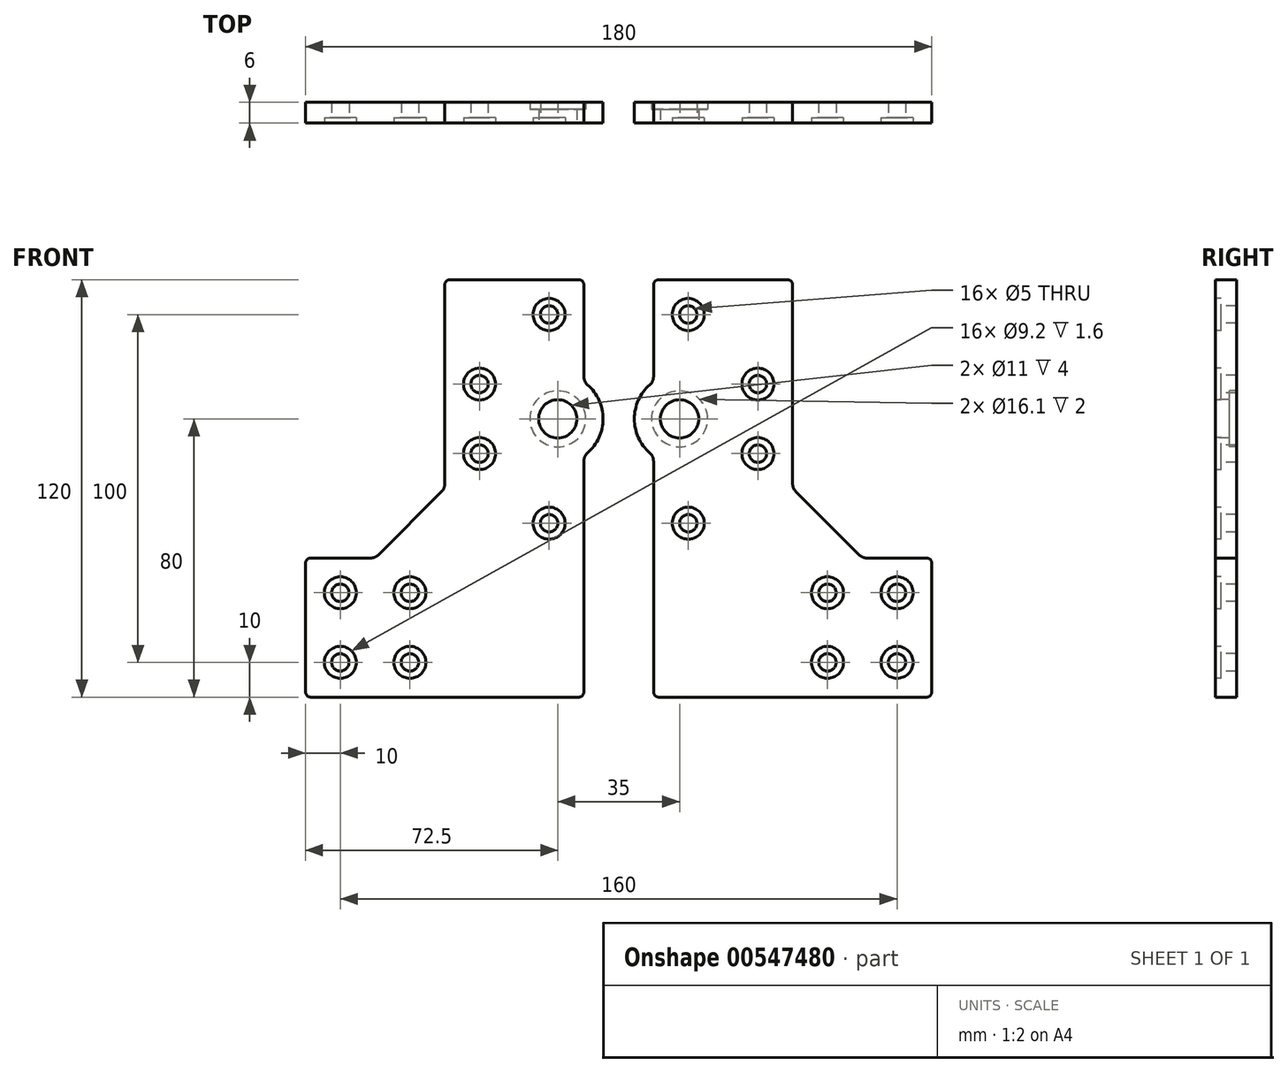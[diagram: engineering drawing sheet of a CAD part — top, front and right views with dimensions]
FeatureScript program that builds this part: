
annotation { "Feature Type Name" : "Feature", "Feature Type Description" : "" }
export const myFeature = defineFeature(function(context is Context, id is Id, definition is map)
    precondition{}
    {
        {
            var Q0;
            Q0=qCreatedBy(makeId("Front.planeOp"),FACE);
            var sketch = newSketch(context, id + "F0", { "sketchPlane" : qUnion([Q0])});
            skCircle(sketch, "E0", {"center": v(-80, -70) * mm, "radius": 2.5 * mm});
            skCircle(sketch, "E1", {"center": v(-80, -70) * mm, "radius": 4.6 * mm});
            skCircle(sketch, "E2.0.1.0", {"center": v(-80, -50) * mm, "radius": 2.5 * mm});
            skCircle(sketch, "E2.0.1.1", {"center": v(-80, -50) * mm, "radius": 4.6 * mm});
            skCircle(sketch, "E2.1.0.0", {"center": v(-60, -70) * mm, "radius": 2.5 * mm});
            skCircle(sketch, "E2.1.0.1", {"center": v(-60, -70) * mm, "radius": 4.6 * mm});
            skCircle(sketch, "E2.1.1.0", {"center": v(-60, -50) * mm, "radius": 2.5 * mm});
            skCircle(sketch, "E2.1.1.1", {"center": v(-60, -50) * mm, "radius": 4.6 * mm});
            skCircle(sketch, "E2.2.3.0", {"center": v(-40, -10) * mm, "radius": 2.5 * mm});
            skCircle(sketch, "E2.2.3.1", {"center": v(-40, -10) * mm, "radius": 4.6 * mm});
            skCircle(sketch, "E2.2.4.0", {"center": v(-40, 10) * mm, "radius": 2.5 * mm});
            skCircle(sketch, "E2.2.4.1", {"center": v(-40, 10) * mm, "radius": 4.6 * mm});
            skCircle(sketch, "E2.3.2.0", {"center": v(-20, -30) * mm, "radius": 2.5 * mm});
            skCircle(sketch, "E2.3.2.1", {"center": v(-20, -30) * mm, "radius": 4.6 * mm});
            skCircle(sketch, "E2.3.5.0", {"center": v(-20, 30) * mm, "radius": 2.5 * mm});
            skCircle(sketch, "E2.3.5.1", {"center": v(-20, 30) * mm, "radius": 4.6 * mm});
            skLineSegment(sketch, "E2.direction1", {"start": v(-80, -70) * mm, "end": v(-60, -70) * mm, "construction": true});
            skLineSegment(sketch, "E2.direction2", {"start": v(-80, -70) * mm, "end": v(-80, -50) * mm, "construction": true});
            skLineSegment(sketch, "E3", {"start": v(-90, -80) * mm, "end": v(-10, -80) * mm});
            skLineSegment(sketch, "E4", {"start": v(-10, -80) * mm, "end": v(-10, -10.62) * mm});
            skLineSegment(sketch, "E5", {"start": v(-10, 40) * mm, "end": v(-50, 40) * mm});
            skLineSegment(sketch, "E6", {"start": v(-50, 40) * mm, "end": v(-50, -20) * mm});
            skLineSegment(sketch, "E7", {"start": v(-70, -40) * mm, "end": v(-90, -40) * mm});
            skLineSegment(sketch, "E8", {"start": v(-90, -40) * mm, "end": v(-90, -80) * mm});
            skCircle(sketch, "E9", {"center": v(-17.5, 0) * mm, "radius": 5.5 * mm});
            skCircle(sketch, "E10", {"center": v(-17.5, 0) * mm, "radius": 8.05 * mm});
            skArc(sketch, "E11", {"start": v(-10, -10.62) * mm, "mid": v(-4.5, 0) * mm, "end": v(-10, 10.62) * mm});
            skLineSegment(sketch, "E12.trimOffspring", {"start": v(-10, 10.62) * mm, "end": v(-10, 40) * mm});
            skLineSegment(sketch, "E13", {"start": v(-70, -40) * mm, "end": v(-50, -20) * mm});
            skSolve(sketch);
        }
        {
            var Q0;
            Q0=makeQuery(id+"F0.imprint","IMPRINT",FACE,{"disambiguationData":[TD([[makeQuery(id+"F0.imprint","IMPRINT",EDGE,{"derivedFrom":sQuery(id+"F0.wireOp",EDGE,"E1")}),-1.0]])]});
            var Q1;
            Q1=makeQuery(id+"F0.imprint","IMPRINT",FACE,{"disambiguationData":[TD([[makeQuery(id+"F0.imprint","IMPRINT",EDGE,{"derivedFrom":sQuery(id+"F0.wireOp",EDGE,"E2.3.5.0")}),-1.0]])]});
            var Q2;
            Q2=makeQuery(id+"F0.imprint","IMPRINT",FACE,{"disambiguationData":[TD([[makeQuery(id+"F0.imprint","IMPRINT",EDGE,{"derivedFrom":sQuery(id+"F0.wireOp",EDGE,"E2.2.4.0")}),-1.0]])]});
            var Q3;
            Q3=makeQuery(id+"F0.imprint","IMPRINT",FACE,{"disambiguationData":[TD([[makeQuery(id+"F0.imprint","IMPRINT",EDGE,{"derivedFrom":sQuery(id+"F0.wireOp",EDGE,"E2.2.3.0")}),-1.0]])]});
            var Q4;
            Q4=makeQuery(id+"F0.imprint","IMPRINT",FACE,{"disambiguationData":[TD([[makeQuery(id+"F0.imprint","IMPRINT",EDGE,{"derivedFrom":sQuery(id+"F0.wireOp",EDGE,"E9")}),-1.0]])]});
            var Q5;
            Q5=makeQuery(id+"F0.imprint","IMPRINT",FACE,{"disambiguationData":[TD([[makeQuery(id+"F0.imprint","IMPRINT",EDGE,{"derivedFrom":sQuery(id+"F0.wireOp",EDGE,"E2.3.2.0")}),-1.0]])]});
            var Q6;
            Q6=makeQuery(id+"F0.imprint","IMPRINT",FACE,{"disambiguationData":[TD([[makeQuery(id+"F0.imprint","IMPRINT",EDGE,{"derivedFrom":sQuery(id+"F0.wireOp",EDGE,"E2.1.1.0")}),-1.0]])]});
            var Q7;
            Q7=makeQuery(id+"F0.imprint","IMPRINT",FACE,{"disambiguationData":[TD([[makeQuery(id+"F0.imprint","IMPRINT",EDGE,{"derivedFrom":sQuery(id+"F0.wireOp",EDGE,"E2.0.1.0")}),-1.0]])]});
            var Q8;
            Q8=makeQuery(id+"F0.imprint","IMPRINT",FACE,{"disambiguationData":[TD([[makeQuery(id+"F0.imprint","IMPRINT",EDGE,{"derivedFrom":sQuery(id+"F0.wireOp",EDGE,"E0")}),-1.0]])]});
            var Q9;
            Q9=makeQuery(id+"F0.imprint","IMPRINT",FACE,{"disambiguationData":[TD([[makeQuery(id+"F0.imprint","IMPRINT",EDGE,{"derivedFrom":sQuery(id+"F0.wireOp",EDGE,"E2.1.0.0")}),-1.0]])]});
            extrude(context, id + "F1", {"entities" : qUnion([Q0, Q1, Q2, Q3, Q4, Q5, Q6, Q7, Q8, Q9]), "oppositeDirection" : true, "depth" : 6 * mm, "offsetDistance" : 25 * mm});
        }
        {
            var Q0;
            Q0=makeQuery(id+"F0.imprint","IMPRINT",FACE,{"disambiguationData":[TD([[makeQuery(id+"F0.imprint","IMPRINT",EDGE,{"derivedFrom":sQuery(id+"F0.wireOp",EDGE,"E2.3.5.0")}),-1.0]])]});
            var Q1;
            Q1=makeQuery(id+"F0.imprint","IMPRINT",FACE,{"disambiguationData":[TD([[makeQuery(id+"F0.imprint","IMPRINT",EDGE,{"derivedFrom":sQuery(id+"F0.wireOp",EDGE,"E2.2.4.0")}),-1.0]])]});
            var Q2;
            Q2=makeQuery(id+"F0.imprint","IMPRINT",FACE,{"disambiguationData":[TD([[makeQuery(id+"F0.imprint","IMPRINT",EDGE,{"derivedFrom":sQuery(id+"F0.wireOp",EDGE,"E2.2.3.0")}),-1.0]])]});
            var Q3;
            Q3=makeQuery(id+"F0.imprint","IMPRINT",FACE,{"disambiguationData":[TD([[makeQuery(id+"F0.imprint","IMPRINT",EDGE,{"derivedFrom":sQuery(id+"F0.wireOp",EDGE,"E2.3.2.0")}),-1.0]])]});
            var Q4;
            Q4=makeQuery(id+"F0.imprint","IMPRINT",FACE,{"disambiguationData":[TD([[makeQuery(id+"F0.imprint","IMPRINT",EDGE,{"derivedFrom":sQuery(id+"F0.wireOp",EDGE,"E2.1.1.0")}),-1.0]])]});
            var Q5;
            Q5=makeQuery(id+"F0.imprint","IMPRINT",FACE,{"disambiguationData":[TD([[makeQuery(id+"F0.imprint","IMPRINT",EDGE,{"derivedFrom":sQuery(id+"F0.wireOp",EDGE,"E2.0.1.0")}),-1.0]])]});
            var Q6;
            Q6=makeQuery(id+"F0.imprint","IMPRINT",FACE,{"disambiguationData":[TD([[makeQuery(id+"F0.imprint","IMPRINT",EDGE,{"derivedFrom":sQuery(id+"F0.wireOp",EDGE,"E0")}),-1.0]])]});
            var Q7;
            Q7=makeQuery(id+"F0.imprint","IMPRINT",FACE,{"disambiguationData":[TD([[makeQuery(id+"F0.imprint","IMPRINT",EDGE,{"derivedFrom":sQuery(id+"F0.wireOp",EDGE,"E2.1.0.0")}),-1.0]])]});
            extrude(context, id + "F2", {"entities" : qUnion([Q0, Q1, Q2, Q3, Q4, Q5, Q6, Q7]), "operationType" : NewBodyOperationType.REMOVE, "oppositeDirection" : true, "depth" : 1.6 * mm, "offsetDistance" : 25 * mm});
        }
        {
            var Q0;
            Q0=makeQuery(id+"F0.imprint","IMPRINT",FACE,{"disambiguationData":[TD([[makeQuery(id+"F0.imprint","IMPRINT",EDGE,{"derivedFrom":sQuery(id+"F0.wireOp",EDGE,"E9")}),-1.0]])]});
            extrude(context, id + "F3", {"entities" : qUnion([Q0]), "operationType" : NewBodyOperationType.REMOVE, "oppositeDirection" : true, "depth" : 6 * mm, "offsetDistance" : 25 * mm, "hasSecondDirection" : true, "secondDirectionOppositeDirection" : true, "secondDirectionDepth" : 4 * mm});
        }
        {
            var Q0;
            Q0=makeQuery(id+"F1.opExtrude","SWEPT_EDGE",EDGE,{"disambiguationData":[OSD([sQuery(id+"F0.wireOp",EDGE,"E5"),sQuery(id+"F0.wireOp",EDGE,"E12.trimOffspring")])]});
            var Q1;
            Q1=makeQuery(id+"F1.opExtrude","SWEPT_EDGE",EDGE,{"disambiguationData":[OSD([sQuery(id+"F0.wireOp",EDGE,"E5"),sQuery(id+"F0.wireOp",EDGE,"E6")])]});
            var Q2;
            Q2=makeQuery(id+"F1.opExtrude","SWEPT_EDGE",EDGE,{"disambiguationData":[OSD([sQuery(id+"F0.wireOp",EDGE,"E7"),sQuery(id+"F0.wireOp",EDGE,"E8")])]});
            var Q3;
            Q3=makeQuery(id+"F1.opExtrude","SWEPT_EDGE",EDGE,{"disambiguationData":[OSD([sQuery(id+"F0.wireOp",EDGE,"E3"),sQuery(id+"F0.wireOp",EDGE,"E8")])]});
            var Q4;
            Q4=makeQuery(id+"F1.opExtrude","SWEPT_EDGE",EDGE,{"disambiguationData":[OSD([sQuery(id+"F0.wireOp",EDGE,"E3"),sQuery(id+"F0.wireOp",EDGE,"E4")])]});
            fillet(context, id + "F4", {"entities" : qUnion([Q0, Q1, Q2, Q3, Q4]), "radius" : 1.5 * mm, "tangentPropagation" : true, "allowEdgeOverflow" : false});
        }
        {
            var Q0;
            Q0=makeQuery(id+"F1.opExtrude","SWEPT_EDGE",EDGE,{"disambiguationData":[OSD([sQuery(id+"F0.wireOp",EDGE,"E7"),sQuery(id+"F0.wireOp",EDGE,"E13")])]});
            var Q1;
            Q1=makeQuery(id+"F1.opExtrude","SWEPT_EDGE",EDGE,{"disambiguationData":[OSD([sQuery(id+"F0.wireOp",EDGE,"E6"),sQuery(id+"F0.wireOp",EDGE,"E13")])]});
            var Q2;
            Q2=makeQuery(id+"F1.opExtrude","SWEPT_EDGE",EDGE,{"disambiguationData":[OSD([sQuery(id+"F0.wireOp",EDGE,"E11"),sQuery(id+"F0.wireOp",EDGE,"E12.trimOffspring")])]});
            var Q3;
            Q3=makeQuery(id+"F1.opExtrude","SWEPT_EDGE",EDGE,{"disambiguationData":[OSD([sQuery(id+"F0.wireOp",EDGE,"E4"),sQuery(id+"F0.wireOp",EDGE,"E11")])]});
            fillet(context, id + "F5", {"entities" : qUnion([Q0, Q1, Q2, Q3]), "radius" : 3 * mm, "tangentPropagation" : true, "allowEdgeOverflow" : false});
        }
        {
            var Q0;
            Q0=makeQuery(id+"F1.opExtrude","SWEPT_BODY",BODY,{"disambiguationData":[OSD([sQuery(id+"F0.wireOp",EDGE,"E0"),sQuery(id+"F0.wireOp",EDGE,"E2.0.1.0"),sQuery(id+"F0.wireOp",EDGE,"E2.1.0.0"),sQuery(id+"F0.wireOp",EDGE,"E2.1.1.0"),sQuery(id+"F0.wireOp",EDGE,"E2.2.3.0"),sQuery(id+"F0.wireOp",EDGE,"E2.2.4.0"),sQuery(id+"F0.wireOp",EDGE,"E2.3.2.0"),sQuery(id+"F0.wireOp",EDGE,"E2.3.5.0"),sQuery(id+"F0.wireOp",EDGE,"E3"),sQuery(id+"F0.wireOp",EDGE,"E4"),sQuery(id+"F0.wireOp",EDGE,"E5"),sQuery(id+"F0.wireOp",EDGE,"E6"),sQuery(id+"F0.wireOp",EDGE,"E7"),sQuery(id+"F0.wireOp",EDGE,"E8"),sQuery(id+"F0.wireOp",EDGE,"E9"),sQuery(id+"F0.wireOp",EDGE,"E11"),sQuery(id+"F0.wireOp",EDGE,"E12.trimOffspring"),sQuery(id+"F0.wireOp",EDGE,"E13")])]});
            var Q1;
            Q1=qCreatedBy(makeId("Right.planeOp"),FACE);
            mirror(context, id + "F6", {"entities" : qUnion([Q0]), "mirrorPlane" : qUnion([Q1])});
        }
    });
